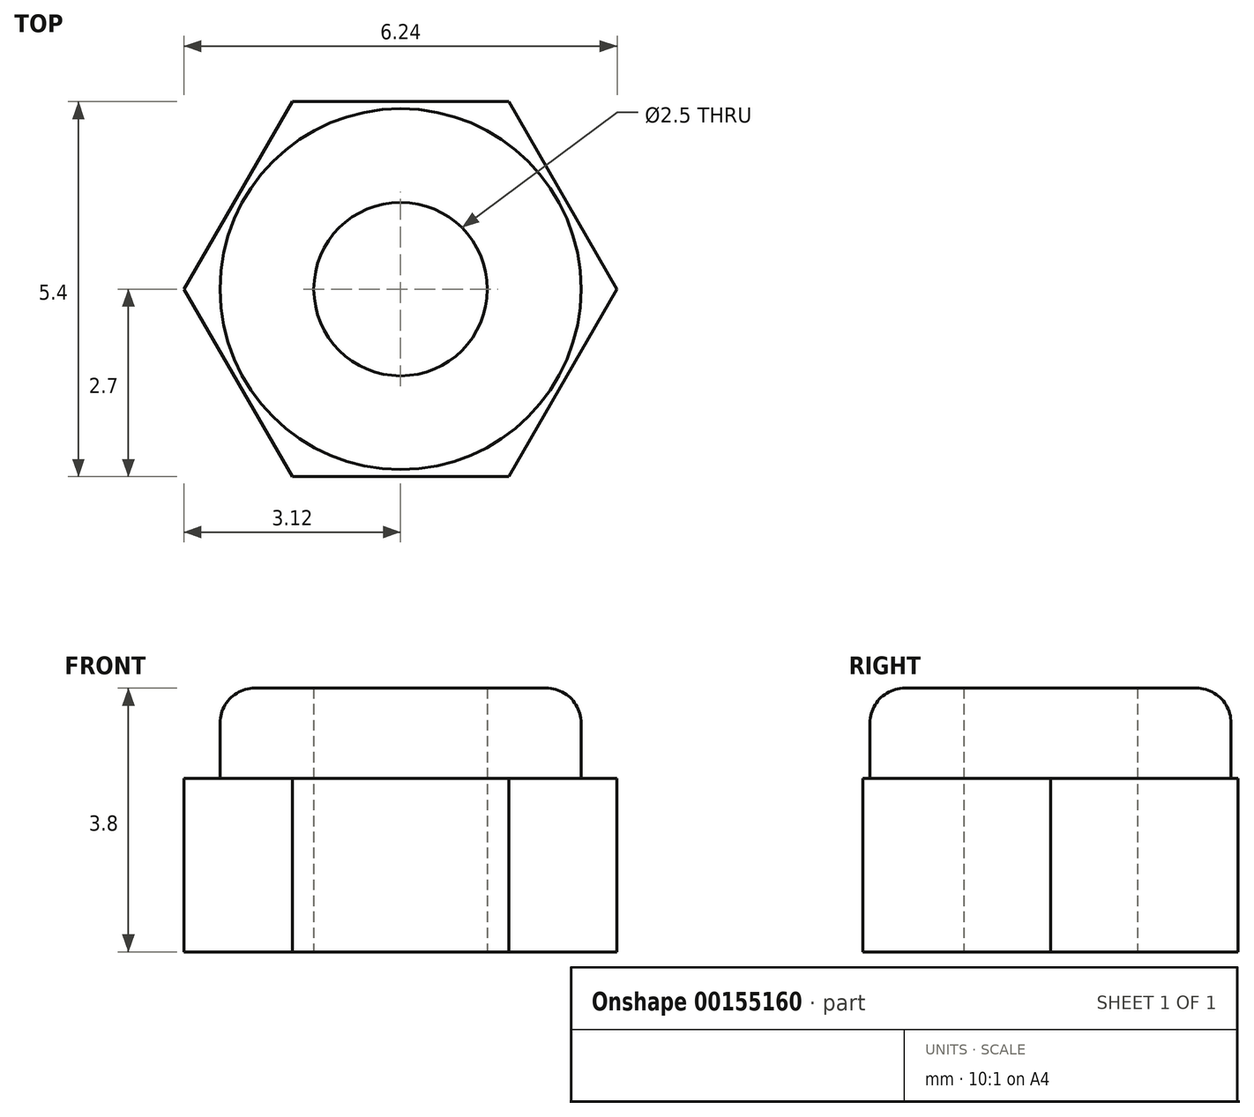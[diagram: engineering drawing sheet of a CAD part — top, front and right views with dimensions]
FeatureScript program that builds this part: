
annotation { "Feature Type Name" : "Feature", "Feature Type Description" : "" }
export const myFeature = defineFeature(function(context is Context, id is Id, definition is map)
    precondition{}
    {
        {
            var Q0;
            Q0=qCreatedBy(makeId("Top.planeOp"),FACE);
            var sketch = newSketch(context, id + "F0", { "sketchPlane" : qUnion([Q0])});
            skCircle(sketch, "E0.cCircle", {"center": v(0, 0) * mm, "radius": 2.7 * mm, "construction": true});
            skLineSegment(sketch, "E0.0", {"start": v(1.56, -2.7) * mm, "end": v(-1.56, -2.7) * mm});
            skLineSegment(sketch, "E0.1", {"start": v(-1.56, -2.7) * mm, "end": v(-3.12, 0) * mm});
            skLineSegment(sketch, "E0.2", {"start": v(-3.12, 0) * mm, "end": v(-1.56, 2.7) * mm});
            skLineSegment(sketch, "E0.3", {"start": v(-1.56, 2.7) * mm, "end": v(1.56, 2.7) * mm});
            skLineSegment(sketch, "E0.4", {"start": v(1.56, 2.7) * mm, "end": v(3.12, 0) * mm});
            skLineSegment(sketch, "E0.5", {"start": v(3.12, 0) * mm, "end": v(1.56, -2.7) * mm});
            skPoint(sketch, "E0.0.midPoint", {"position": v(0, -2.7) * mm});
            skSolve(sketch);
        }
        {
            var Q0;
            Q0=makeQuery(id+"F0.imprint","IMPRINT",FACE,{"disambiguationData":[TD([[makeQuery(id+"F0.imprint","IMPRINT",EDGE,{"derivedFrom":sQuery(id+"F0.wireOp",EDGE,"E0.0")}),-1.0]])]});
            extrude(context, id + "F1", {"entities" : qUnion([Q0]), "depth" : 2.5 * mm});
        }
        {
            var Q0;
            Q0=makeQuery(id+"F1.opExtrude","CAP_FACE",FACE,{"disambiguationData":[OSD([sQuery(id+"F0.wireOp",EDGE,"E0.0"),sQuery(id+"F0.wireOp",EDGE,"E0.1"),sQuery(id+"F0.wireOp",EDGE,"E0.2"),sQuery(id+"F0.wireOp",EDGE,"E0.3"),sQuery(id+"F0.wireOp",EDGE,"E0.4"),sQuery(id+"F0.wireOp",EDGE,"E0.5")])],"isStart":true});
            var sketch = newSketch(context, id + "F2", { "sketchPlane" : qUnion([Q0])});
            skCircle(sketch, "E1", {"center": v(0, 0) * mm, "radius": 2.6 * mm});
            skCircle(sketch, "E2", {"center": v(0, 0) * mm, "radius": 1.25 * mm});
            skSolve(sketch);
        }
        {
            var Q0;
            Q0=makeQuery(id+"F2.imprint","IMPRINT",FACE,{"disambiguationData":[TD([[makeQuery(id+"F2.imprint","IMPRINT",EDGE,{"derivedFrom":sQuery(id+"F2.wireOp",EDGE,"E1")}),1.0]])]});
            extrude(context, id + "F3", {"entities" : qUnion([Q0]), "operationType" : NewBodyOperationType.ADD, "oppositeDirection" : true, "depth" : 3.8 * mm});
        }
        {
            var Q0;
            Q0=makeQuery(id+"F2.imprint","IMPRINT",FACE,{"disambiguationData":[TD([[makeQuery(id+"F2.imprint","IMPRINT",EDGE,{"derivedFrom":sQuery(id+"F2.wireOp",EDGE,"E2")}),1.0]])]});
            extrude(context, id + "F4", {"entities" : qUnion([Q0]), "operationType" : NewBodyOperationType.REMOVE, "oppositeDirection" : true, "depth" : 25 * mm});
        }
        {
            var Q0;
            Q0=makeQuery(id+"F3.opExtrude","CAP_EDGE",EDGE,{"disambiguationData":[OSD([sQuery(id+"F2.wireOp",EDGE,"E1")])],"isStart":false});
            fillet(context, id + "F5", {"entities" : qUnion([Q0]), "radius" : 0.5 * mm, "tangentPropagation" : true, "allowEdgeOverflow" : false});
        }
    });
